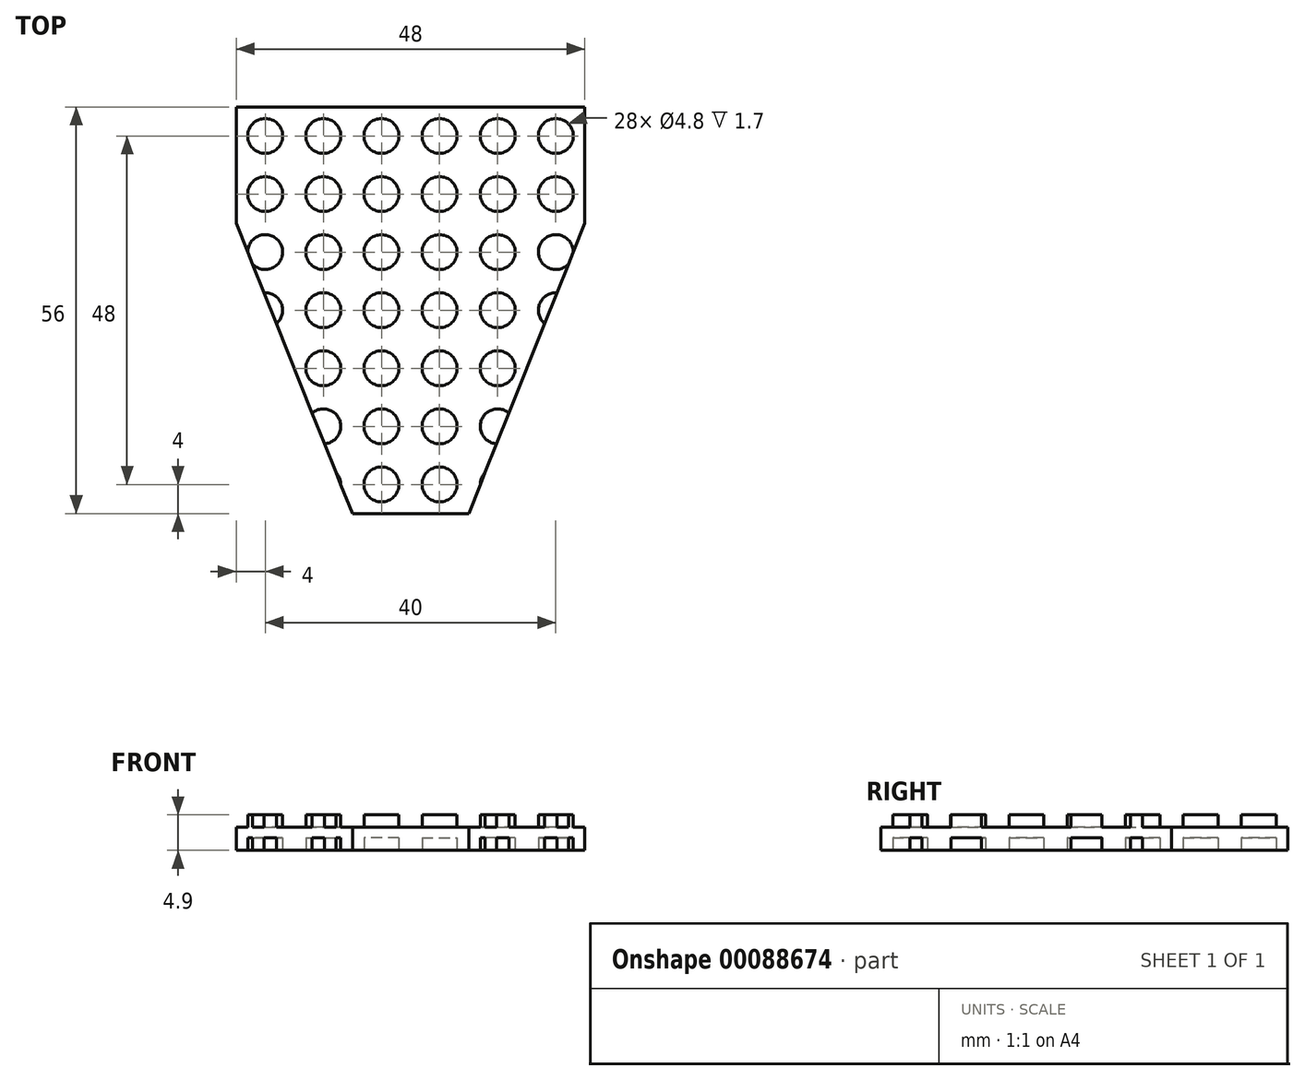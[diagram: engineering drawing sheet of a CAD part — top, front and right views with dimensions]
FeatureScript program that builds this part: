
annotation { "Feature Type Name" : "Feature", "Feature Type Description" : "" }
export const myFeature = defineFeature(function(context is Context, id is Id, definition is map)
    precondition{}
    {
        {
            var Q0;
            Q0=qCreatedBy(makeId("Front.planeOp"),FACE);
            var sketch = newSketch(context, id + "F0", { "sketchPlane" : qUnion([Q0])});
            skLineSegment(sketch, "E0.bottom", {"start": v(-4, 3.2) * mm, "end": v(-2.4, 3.2) * mm});
            skLineSegment(sketch, "E0.top", {"start": v(-4, 0) * mm, "end": v(4, 0) * mm});
            skLineSegment(sketch, "E0.left", {"start": v(-4, 3.2) * mm, "end": v(-4, 0) * mm});
            skLineSegment(sketch, "E0.right", {"start": v(4, 3.2) * mm, "end": v(4, 0) * mm});
            skLineSegment(sketch, "E1.top", {"start": v(-2.4, 4.9) * mm, "end": v(2.4, 4.9) * mm});
            skLineSegment(sketch, "E1.left", {"start": v(-2.4, 3.2) * mm, "end": v(-2.4, 4.9) * mm});
            skLineSegment(sketch, "E1.right", {"start": v(2.4, 3.2) * mm, "end": v(2.4, 4.9) * mm});
            skLineSegment(sketch, "E2", {"start": v(0, 0) * mm, "end": v(0, 24.04) * mm, "construction": true});
            skLineSegment(sketch, "E3.trimOffspring", {"start": v(2.4, 3.2) * mm, "end": v(4, 3.2) * mm});
            skSolve(sketch);
        }
        {
            var Q0;
            Q0=makeQuery(id+"F0.imprint","IMPRINT",FACE,{"disambiguationData":[TD([[makeQuery(id+"F0.imprint","IMPRINT",EDGE,{"derivedFrom":sQuery(id+"F0.wireOp",EDGE,"E0.bottom")}),-1.0]])]});
            extrude(context, id + "F1", {"entities" : qUnion([Q0]), "depth" : 8 * mm});
        }
        {
            var Q0;
            Q0=qCreatedBy(makeId("Top.planeOp"),FACE);
            var Q1;
            Q1=makeQuery(id+"F1.opExtrude","CAP_VERTEX",VERTEX,{"disambiguationData":[OSD([sQuery(id+"F0.wireOp",EDGE,"E1.top"),sQuery(id+"F0.wireOp",EDGE,"E1.right")])],"isStart":true});
            cPlane(context, id + "F2", {"entities" : qUnion([Q0, Q1]), "cplaneType" : CPlaneType.PLANE_POINT, "offset" : 152.4 * mm, "width" : 152.4 * mm, "height" : 152.4 * mm});
        }
        {
            var Q0;
            Q0=qCreatedBy(id+"F2.planeOp",FACE);
            var sketch = newSketch(context, id + "F3", { "sketchPlane" : qUnion([Q0])});
            skLineSegment(sketch, "E4.0", {"start": v(-4, -8) * mm, "end": v(-4, 0) * mm});
            skLineSegment(sketch, "E5.0", {"start": v(4, -8) * mm, "end": v(4, 0) * mm});
            skLineSegment(sketch, "E6", {"start": v(-4, 0) * mm, "end": v(4, 0) * mm});
            skLineSegment(sketch, "E7", {"start": v(-4, -8) * mm, "end": v(4, -8) * mm});
            skLineSegment(sketch, "E8", {"start": v(-4, 0) * mm, "end": v(4, -8) * mm, "construction": true});
            skLineSegment(sketch, "E9", {"start": v(-4, -8) * mm, "end": v(4, 0) * mm, "construction": true});
            skCircle(sketch, "E10", {"center": v(0, -4) * mm, "radius": 2.4 * mm});
            skSolve(sketch);
        }
        {
            var Q0;
            Q0=qSketchRegion(id+"F3",true);
            var Q1;
            Q1=makeQuery(id+"F1.opExtrude","SWEPT_FACE",FACE,{"disambiguationData":[OSD([sQuery(id+"F0.wireOp",EDGE,"E0.bottom")])]});
            extrude(context, id + "F4", {"entities" : qUnion([Q0]), "operationType" : NewBodyOperationType.REMOVE, "endBound" : BoundingType.UP_TO_SURFACE, "oppositeDirection" : true, "endBoundEntityFace" : qUnion([Q1]), "depth" : 25.4 * mm});
        }
        {
            var Q0;
            Q0=qCreatedBy(makeId("Top.planeOp"),FACE);
            var sketch = newSketch(context, id + "F5", { "sketchPlane" : qUnion([Q0])});
            skCircle(sketch, "E11.0", {"center": v(0, -4) * mm, "radius": 2.4 * mm});
            skSolve(sketch);
        }
        {
            var Q0;
            Q0=makeQuery(id+"F5.imprint","IMPRINT",FACE,{"disambiguationData":[TD([[makeQuery(id+"F5.imprint","IMPRINT",EDGE,{"derivedFrom":sQuery(id+"F5.wireOp",EDGE,"E11.0")}),1.0]])]});
            extrude(context, id + "F6", {"entities" : qUnion([Q0]), "operationType" : NewBodyOperationType.REMOVE, "depth" : 1.7 * mm});
        }
        {
            var Q0;
            Q0=qCreatedBy(makeId("Right.planeOp"),FACE);
            var Q1;
            Q1=makeQuery(id+"F1.opExtrude","CAP_VERTEX",VERTEX,{"disambiguationData":[OSD([sQuery(id+"F0.wireOp",EDGE,"E0.right"),sQuery(id+"F0.wireOp",EDGE,"E3.trimOffspring")])],"isStart":false});
            cPlane(context, id + "F7", {"entities" : qUnion([Q0, Q1]), "cplaneType" : CPlaneType.PLANE_POINT, "offset" : 152.4 * mm, "width" : 152.4 * mm, "height" : 152.4 * mm});
        }
        {
            var Q0;
            Q0=makeQuery(id+"F1.opExtrude","SWEPT_BODY",BODY,{"disambiguationData":[OSD([sQuery(id+"F0.wireOp",EDGE,"E0.bottom"),sQuery(id+"F0.wireOp",EDGE,"E0.top"),sQuery(id+"F0.wireOp",EDGE,"E0.left"),sQuery(id+"F0.wireOp",EDGE,"E0.right"),sQuery(id+"F0.wireOp",EDGE,"E1.top"),sQuery(id+"F0.wireOp",EDGE,"E1.left"),sQuery(id+"F0.wireOp",EDGE,"E1.right"),sQuery(id+"F0.wireOp",EDGE,"E3.trimOffspring")])]});
            var Q1;
            Q1=qCreatedBy(id+"F7.planeOp",FACE);
            mirror(context, id + "F8", {"operationType" : NewBodyOperationType.ADD, "entities" : qUnion([Q0]), "mirrorPlane" : qUnion([Q1])});
        }
        {
            var Q0;
            Q0=qCreatedBy(id+"F7.planeOp",FACE);
            var Q1;
            Q1=makeQuery(id+"F8.opPattern","COPY",VERTEX,{"derivedFrom":makeQuery(id+"F1.opExtrude","CAP_VERTEX",VERTEX,{"disambiguationData":[OSD([sQuery(id+"F0.wireOp",EDGE,"E0.bottom"),sQuery(id+"F0.wireOp",EDGE,"E0.left")])],"isStart":false}),"instanceName":"1"});
            cPlane(context, id + "F9", {"entities" : qUnion([Q0, Q1]), "cplaneType" : CPlaneType.PLANE_POINT, "offset" : 152.4 * mm, "width" : 152.4 * mm, "height" : 152.4 * mm});
        }
        {
            var Q0;
            Q0=makeQuery(id+"F1.opExtrude","SWEPT_BODY",BODY,{"disambiguationData":[OSD([sQuery(id+"F0.wireOp",EDGE,"E0.bottom"),sQuery(id+"F0.wireOp",EDGE,"E0.top"),sQuery(id+"F0.wireOp",EDGE,"E0.left"),sQuery(id+"F0.wireOp",EDGE,"E0.right"),sQuery(id+"F0.wireOp",EDGE,"E1.top"),sQuery(id+"F0.wireOp",EDGE,"E1.left"),sQuery(id+"F0.wireOp",EDGE,"E1.right"),sQuery(id+"F0.wireOp",EDGE,"E3.trimOffspring")])]});
            var Q1;
            Q1=qCreatedBy(id+"F9.planeOp",FACE);
            mirror(context, id + "F10", {"operationType" : NewBodyOperationType.ADD, "entities" : qUnion([Q0]), "mirrorPlane" : qUnion([Q1])});
        }
        {
            var Q0;
            Q0=qCreatedBy(makeId("Right.planeOp"),FACE);
            var Q1;
            Q1=makeQuery(id+"F10.opPattern","COPY",VERTEX,{"derivedFrom":makeQuery(id+"F1.opExtrude","CAP_VERTEX",VERTEX,{"disambiguationData":[OSD([sQuery(id+"F0.wireOp",EDGE,"E0.bottom"),sQuery(id+"F0.wireOp",EDGE,"E0.left")])],"isStart":false}),"instanceName":"1"});
            cPlane(context, id + "F11", {"entities" : qUnion([Q0, Q1]), "cplaneType" : CPlaneType.PLANE_POINT, "offset" : 152.4 * mm, "width" : 152.4 * mm, "height" : 152.4 * mm});
        }
        {
            var Q0;
            Q0=makeQuery(id+"F1.opExtrude","SWEPT_BODY",BODY,{"disambiguationData":[OSD([sQuery(id+"F0.wireOp",EDGE,"E0.bottom"),sQuery(id+"F0.wireOp",EDGE,"E0.top"),sQuery(id+"F0.wireOp",EDGE,"E0.left"),sQuery(id+"F0.wireOp",EDGE,"E0.right"),sQuery(id+"F0.wireOp",EDGE,"E1.top"),sQuery(id+"F0.wireOp",EDGE,"E1.left"),sQuery(id+"F0.wireOp",EDGE,"E1.right"),sQuery(id+"F0.wireOp",EDGE,"E3.trimOffspring")])]});
            var Q1;
            Q1=qCreatedBy(id+"F11.planeOp",FACE);
            mirror(context, id + "F12", {"operationType" : NewBodyOperationType.ADD, "entities" : qUnion([Q0]), "mirrorPlane" : qUnion([Q1])});
        }
        {
            var Q0;
            Q0=makeQuery(id+"F1.opExtrude","SWEPT_BODY",BODY,{"disambiguationData":[OSD([sQuery(id+"F0.wireOp",EDGE,"E0.bottom"),sQuery(id+"F0.wireOp",EDGE,"E0.top"),sQuery(id+"F0.wireOp",EDGE,"E0.left"),sQuery(id+"F0.wireOp",EDGE,"E0.right"),sQuery(id+"F0.wireOp",EDGE,"E1.top"),sQuery(id+"F0.wireOp",EDGE,"E1.left"),sQuery(id+"F0.wireOp",EDGE,"E1.right"),sQuery(id+"F0.wireOp",EDGE,"E3.trimOffspring")])]});
            var Q1;
            {var subQ0=makeQuery(id+"F1.opExtrude","CAP_FACE",FACE,{"disambiguationData":[OSD([sQuery(id+"F0.wireOp",EDGE,"E0.bottom"),sQuery(id+"F0.wireOp",EDGE,"E0.top"),sQuery(id+"F0.wireOp",EDGE,"E0.left"),sQuery(id+"F0.wireOp",EDGE,"E0.right"),sQuery(id+"F0.wireOp",EDGE,"E1.top"),sQuery(id+"F0.wireOp",EDGE,"E1.left"),sQuery(id+"F0.wireOp",EDGE,"E1.right"),sQuery(id+"F0.wireOp",EDGE,"E3.trimOffspring")])],"isStart":false});var subQ1=makeQuery(id+"F8.boolean.opBoolean","MERGE",FACE,{"derivedFrom":[subQ0,makeQuery(id+"F8.opPattern","COPY",FACE,{"derivedFrom":subQ0,"instanceName":"1"})]});var subQ2=makeQuery(id+"F10.boolean.opBoolean","MERGE",FACE,{"derivedFrom":[subQ1,makeQuery(id+"F10.opPattern","COPY",FACE,{"derivedFrom":subQ1,"instanceName":"1"})]});Q1=makeQuery(id+"F12.boolean.opBoolean","MERGE",FACE,{"derivedFrom":[subQ2,makeQuery(id+"F12.opPattern","COPY",FACE,{"derivedFrom":subQ2,"instanceName":"1"})]});}
            mirror(context, id + "F13", {"operationType" : NewBodyOperationType.ADD, "entities" : qUnion([Q0]), "mirrorPlane" : qUnion([Q1])});
        }
        {
            var Q0;
            Q0=makeQuery(id+"F1.opExtrude","SWEPT_BODY",BODY,{"disambiguationData":[OSD([sQuery(id+"F0.wireOp",EDGE,"E0.bottom"),sQuery(id+"F0.wireOp",EDGE,"E0.top"),sQuery(id+"F0.wireOp",EDGE,"E0.left"),sQuery(id+"F0.wireOp",EDGE,"E0.right"),sQuery(id+"F0.wireOp",EDGE,"E1.top"),sQuery(id+"F0.wireOp",EDGE,"E1.left"),sQuery(id+"F0.wireOp",EDGE,"E1.right"),sQuery(id+"F0.wireOp",EDGE,"E3.trimOffspring")])]});
            var Q1;
            {var subQ0=makeQuery(id+"F1.opExtrude","CAP_FACE",FACE,{"disambiguationData":[OSD([sQuery(id+"F0.wireOp",EDGE,"E0.bottom"),sQuery(id+"F0.wireOp",EDGE,"E0.top"),sQuery(id+"F0.wireOp",EDGE,"E0.left"),sQuery(id+"F0.wireOp",EDGE,"E0.right"),sQuery(id+"F0.wireOp",EDGE,"E1.top"),sQuery(id+"F0.wireOp",EDGE,"E1.left"),sQuery(id+"F0.wireOp",EDGE,"E1.right"),sQuery(id+"F0.wireOp",EDGE,"E3.trimOffspring")])],"isStart":true});var subQ1=makeQuery(id+"F8.boolean.opBoolean","MERGE",FACE,{"derivedFrom":[subQ0,makeQuery(id+"F8.opPattern","COPY",FACE,{"derivedFrom":subQ0,"instanceName":"1"})]});var subQ2=makeQuery(id+"F10.boolean.opBoolean","MERGE",FACE,{"derivedFrom":[subQ1,makeQuery(id+"F10.opPattern","COPY",FACE,{"derivedFrom":subQ1,"instanceName":"1"})]});Q1=makeQuery(id+"F13.opPattern","COPY",FACE,{"derivedFrom":makeQuery(id+"F12.boolean.opBoolean","MERGE",FACE,{"derivedFrom":[subQ2,makeQuery(id+"F12.opPattern","COPY",FACE,{"derivedFrom":subQ2,"instanceName":"1"})]}),"instanceName":"1"});}
            mirror(context, id + "F14", {"operationType" : NewBodyOperationType.ADD, "entities" : qUnion([Q0]), "mirrorPlane" : qUnion([Q1])});
        }
        {
            var Q0;
            Q0=makeQuery(id+"F1.opExtrude","SWEPT_BODY",BODY,{"disambiguationData":[OSD([sQuery(id+"F0.wireOp",EDGE,"E0.bottom"),sQuery(id+"F0.wireOp",EDGE,"E0.top"),sQuery(id+"F0.wireOp",EDGE,"E0.left"),sQuery(id+"F0.wireOp",EDGE,"E0.right"),sQuery(id+"F0.wireOp",EDGE,"E1.top"),sQuery(id+"F0.wireOp",EDGE,"E1.left"),sQuery(id+"F0.wireOp",EDGE,"E1.right"),sQuery(id+"F0.wireOp",EDGE,"E3.trimOffspring")])]});
            var Q1;
            {var subQ0=makeQuery(id+"F1.opExtrude","CAP_FACE",FACE,{"disambiguationData":[OSD([sQuery(id+"F0.wireOp",EDGE,"E0.bottom"),sQuery(id+"F0.wireOp",EDGE,"E0.top"),sQuery(id+"F0.wireOp",EDGE,"E0.left"),sQuery(id+"F0.wireOp",EDGE,"E0.right"),sQuery(id+"F0.wireOp",EDGE,"E1.top"),sQuery(id+"F0.wireOp",EDGE,"E1.left"),sQuery(id+"F0.wireOp",EDGE,"E1.right"),sQuery(id+"F0.wireOp",EDGE,"E3.trimOffspring")])],"isStart":true});var subQ1=makeQuery(id+"F8.boolean.opBoolean","MERGE",FACE,{"derivedFrom":[subQ0,makeQuery(id+"F8.opPattern","COPY",FACE,{"derivedFrom":subQ0,"instanceName":"1"})]});var subQ2=makeQuery(id+"F10.boolean.opBoolean","MERGE",FACE,{"derivedFrom":[subQ1,makeQuery(id+"F10.opPattern","COPY",FACE,{"derivedFrom":subQ1,"instanceName":"1"})]});Q1=makeQuery(id+"F14.opPattern","COPY",FACE,{"derivedFrom":makeQuery(id+"F12.boolean.opBoolean","MERGE",FACE,{"derivedFrom":[subQ2,makeQuery(id+"F12.opPattern","COPY",FACE,{"derivedFrom":subQ2,"instanceName":"1"})]}),"instanceName":"1"});}
            mirror(context, id + "F15", {"operationType" : NewBodyOperationType.ADD, "entities" : qUnion([Q0]), "mirrorPlane" : qUnion([Q1])});
        }
        {
            var Q0;
            Q0=makeQuery(id+"F1.opExtrude","SWEPT_BODY",BODY,{"disambiguationData":[OSD([sQuery(id+"F0.wireOp",EDGE,"E0.bottom"),sQuery(id+"F0.wireOp",EDGE,"E0.top"),sQuery(id+"F0.wireOp",EDGE,"E0.left"),sQuery(id+"F0.wireOp",EDGE,"E0.right"),sQuery(id+"F0.wireOp",EDGE,"E1.top"),sQuery(id+"F0.wireOp",EDGE,"E1.left"),sQuery(id+"F0.wireOp",EDGE,"E1.right"),sQuery(id+"F0.wireOp",EDGE,"E3.trimOffspring")])]});
            var Q1;
            {var subQ0=makeQuery(id+"F1.opExtrude","CAP_FACE",FACE,{"disambiguationData":[OSD([sQuery(id+"F0.wireOp",EDGE,"E0.bottom"),sQuery(id+"F0.wireOp",EDGE,"E0.top"),sQuery(id+"F0.wireOp",EDGE,"E0.left"),sQuery(id+"F0.wireOp",EDGE,"E0.right"),sQuery(id+"F0.wireOp",EDGE,"E1.top"),sQuery(id+"F0.wireOp",EDGE,"E1.left"),sQuery(id+"F0.wireOp",EDGE,"E1.right"),sQuery(id+"F0.wireOp",EDGE,"E3.trimOffspring")])],"isStart":true});var subQ1=makeQuery(id+"F8.boolean.opBoolean","MERGE",FACE,{"derivedFrom":[subQ0,makeQuery(id+"F8.opPattern","COPY",FACE,{"derivedFrom":subQ0,"instanceName":"1"})]});var subQ2=makeQuery(id+"F10.boolean.opBoolean","MERGE",FACE,{"derivedFrom":[subQ1,makeQuery(id+"F10.opPattern","COPY",FACE,{"derivedFrom":subQ1,"instanceName":"1"})]});Q1=makeQuery(id+"F15.opPattern","COPY",FACE,{"derivedFrom":makeQuery(id+"F12.boolean.opBoolean","MERGE",FACE,{"derivedFrom":[subQ2,makeQuery(id+"F12.opPattern","COPY",FACE,{"derivedFrom":subQ2,"instanceName":"1"})]}),"instanceName":"1"});}
            mirror(context, id + "F16", {"operationType" : NewBodyOperationType.ADD, "entities" : qUnion([Q0]), "mirrorPlane" : qUnion([Q1])});
        }
        {
            var Q0;
            {var subQ0=makeQuery(id+"F12.opPattern","COPY",FACE,{"derivedFrom":makeQuery(id+"F1.opExtrude","SWEPT_FACE",FACE,{"disambiguationData":[OSD([sQuery(id+"F0.wireOp",EDGE,"E0.left")])]}),"instanceName":"1"});var subQ1=makeQuery(id+"F13.boolean.opBoolean","MERGE",FACE,{"derivedFrom":[subQ0,makeQuery(id+"F13.opPattern","COPY",FACE,{"derivedFrom":subQ0,"instanceName":"1"})]});var subQ2=makeQuery(id+"F14.boolean.opBoolean","MERGE",FACE,{"derivedFrom":[subQ1,makeQuery(id+"F14.opPattern","COPY",FACE,{"derivedFrom":subQ1,"instanceName":"1"})]});var subQ3=makeQuery(id+"F15.boolean.opBoolean","MERGE",FACE,{"derivedFrom":[subQ2,makeQuery(id+"F15.opPattern","COPY",FACE,{"derivedFrom":subQ2,"instanceName":"1"})]});Q0=makeQuery(id+"F16.boolean.opBoolean","MERGE",FACE,{"derivedFrom":[subQ3,makeQuery(id+"F16.opPattern","COPY",FACE,{"derivedFrom":subQ3,"instanceName":"1"})]});}
            var sketch = newSketch(context, id + "F17", { "sketchPlane" : qUnion([Q0])});
            skLineSegment(sketch, "E12.bottom", {"start": v(20.87, 8.7) * mm, "end": v(-148.87, 8.7) * mm});
            skLineSegment(sketch, "E12.top", {"start": v(20.87, -8.7) * mm, "end": v(-148.87, -8.7) * mm});
            skLineSegment(sketch, "E12.left", {"start": v(20.87, 8.7) * mm, "end": v(20.87, -8.7) * mm});
            skLineSegment(sketch, "E12.right", {"start": v(-148.87, 8.7) * mm, "end": v(-148.87, -8.7) * mm});
            skPoint(sketch, "E12.middle", {"position": v(-64, 0) * mm});
            skSolve(sketch);
        }
        {
            var Q0;
            Q0 = qSketchRegion(id + "F17", true);
            extrude(context, id + "F18", {"entities" : qUnion([Q0]), "operationType" : NewBodyOperationType.REMOVE, "oppositeDirection" : true, "depth" : 16 * mm, "offsetDistance" : 25.4 * mm});
        }
        {
            var Q0;
            {var subQ0=makeQuery(id+"F1.opExtrude","CAP_FACE",FACE,{"disambiguationData":[OSD([sQuery(id+"F0.wireOp",EDGE,"E0.bottom"),sQuery(id+"F0.wireOp",EDGE,"E0.top"),sQuery(id+"F0.wireOp",EDGE,"E0.left"),sQuery(id+"F0.wireOp",EDGE,"E0.right"),sQuery(id+"F0.wireOp",EDGE,"E1.top"),sQuery(id+"F0.wireOp",EDGE,"E1.left"),sQuery(id+"F0.wireOp",EDGE,"E1.right"),sQuery(id+"F0.wireOp",EDGE,"E3.trimOffspring")])],"isStart":true});var subQ1=makeQuery(id+"F8.boolean.opBoolean","MERGE",FACE,{"derivedFrom":[subQ0,makeQuery(id+"F8.opPattern","COPY",FACE,{"derivedFrom":subQ0,"instanceName":"1"})]});var subQ2=makeQuery(id+"F10.boolean.opBoolean","MERGE",FACE,{"derivedFrom":[subQ1,makeQuery(id+"F10.opPattern","COPY",FACE,{"derivedFrom":subQ1,"instanceName":"1"})]});Q0=makeQuery(id+"F16.opPattern","COPY",FACE,{"derivedFrom":makeQuery(id+"F12.boolean.opBoolean","MERGE",FACE,{"derivedFrom":[subQ2,makeQuery(id+"F12.opPattern","COPY",FACE,{"derivedFrom":subQ2,"instanceName":"1"})]}),"instanceName":"1"});}
            var sketch = newSketch(context, id + "F19", { "sketchPlane" : qUnion([Q0])});
            skLineSegment(sketch, "E13.bottom", {"start": v(48.72, 21.08) * mm, "end": v(-8.72, 21.08) * mm});
            skLineSegment(sketch, "E13.top", {"start": v(48.72, -14.68) * mm, "end": v(-8.72, -14.68) * mm});
            skLineSegment(sketch, "E13.left", {"start": v(48.72, 21.08) * mm, "end": v(48.72, -14.68) * mm});
            skLineSegment(sketch, "E13.right", {"start": v(-8.72, 21.08) * mm, "end": v(-8.72, -14.68) * mm});
            skPoint(sketch, "E13.middle", {"position": v(20, 3.2) * mm});
            skSolve(sketch);
        }
        {
            var Q0;
            Q0 = qSketchRegion(id + "F19", true);
            extrude(context, id + "F20", {"entities" : qUnion([Q0]), "operationType" : NewBodyOperationType.REMOVE, "oppositeDirection" : true, "depth" : 0.63 * 76.2 * mm, "offsetDistance" : 25.4 * mm});
        }
        {
            var Q0;
            Q0=qCreatedBy(makeId("Top.planeOp"),FACE);
            var sketch = newSketch(context, id + "F21", { "sketchPlane" : qUnion([Q0])});
            skLineSegment(sketch, "E14.0", {"start": v(-4, -80) * mm, "end": v(-4, -16) * mm});
            skLineSegment(sketch, "E15.0", {"start": v(44, -80) * mm, "end": v(44, -16) * mm});
            skCircle(sketch, "E16.0", {"center": v(8, -52) * mm, "radius": 2.4 * mm, "construction": true});
            skCircle(sketch, "E17.0", {"center": v(8, -60) * mm, "radius": 2.4 * mm, "construction": true});
            skCircle(sketch, "E18.0", {"center": v(32, -52) * mm, "radius": 2.4 * mm, "construction": true});
            skCircle(sketch, "E19.0.0", {"center": v(32, -60) * mm, "radius": 2.4 * mm, "construction": true});
            skLineSegment(sketch, "E20", {"start": v(8, -60) * mm, "end": v(32, -52) * mm, "construction": true});
            skLineSegment(sketch, "E21", {"start": v(32, -60) * mm, "end": v(8, -52) * mm, "construction": true});
            skPoint(sketch, "E22", {"position": v(20, -56) * mm});
            skCircle(sketch, "E23.0", {"center": v(16, -52) * mm, "radius": 2.4 * mm, "construction": true});
            skCircle(sketch, "E24.0", {"center": v(24, -52) * mm, "radius": 2.4 * mm, "construction": true});
            skCircle(sketch, "E25.0", {"center": v(16, -60) * mm, "radius": 2.4 * mm, "construction": true});
            skCircle(sketch, "E26.0", {"center": v(24, -60) * mm, "radius": 2.4 * mm, "construction": true});
            skLineSegment(sketch, "E27", {"start": v(8, -52) * mm, "end": v(16, -60) * mm, "construction": true});
            skLineSegment(sketch, "E28", {"start": v(32, -52) * mm, "end": v(24, -60) * mm, "construction": true});
            skPoint(sketch, "E29", {"position": v(12, -56) * mm});
            skPoint(sketch, "E30", {"position": v(28, -56) * mm});
            skCircle(sketch, "E31.0", {"center": v(0, -12) * mm, "radius": 2.4 * mm, "construction": true});
            skCircle(sketch, "E32.0", {"center": v(0, -20) * mm, "radius": 2.4 * mm, "construction": true});
            skCircle(sketch, "E33.0", {"center": v(40, -12) * mm, "radius": 2.4 * mm, "construction": true});
            skCircle(sketch, "E34.0", {"center": v(40, -20) * mm, "radius": 2.4 * mm, "construction": true});
            skLineSegment(sketch, "E35", {"start": v(0, -20) * mm, "end": v(0, -12) * mm, "construction": true});
            skLineSegment(sketch, "E36", {"start": v(40, -20) * mm, "end": v(40, -12) * mm, "construction": true});
            skPoint(sketch, "E37", {"position": v(0, -16) * mm});
            skPoint(sketch, "E38", {"position": v(40, -16) * mm});
            skPoint(sketch, "E39", {"position": v(-4, -16) * mm});
            skPoint(sketch, "E40", {"position": v(44, -16) * mm});
            skLineSegment(sketch, "E41", {"start": v(-4, -16) * mm, "end": v(12, -56) * mm});
            skLineSegment(sketch, "E42", {"start": v(12, -56) * mm, "end": v(28, -56) * mm});
            skLineSegment(sketch, "E43", {"start": v(28, -56) * mm, "end": v(44, -16) * mm});
            skPoint(sketch, "E44.orphan", {"position": v(-4, 0) * mm});
            skPoint(sketch, "E45.0.end.orphan", {"position": v(44, 0) * mm});
            skLineSegment(sketch, "E46.0", {"start": v(-4, -80) * mm, "end": v(44, -80) * mm});
            skSolve(sketch);
        }
        {
            var Q0;
            Q0 = qSketchRegion(id + "F21", true);
            extrude(context, id + "F22", {"entities" : qUnion([Q0]), "operationType" : NewBodyOperationType.REMOVE, "depth" : 25.4 * mm, "offsetDistance" : 25.4 * mm});
        }
    });
